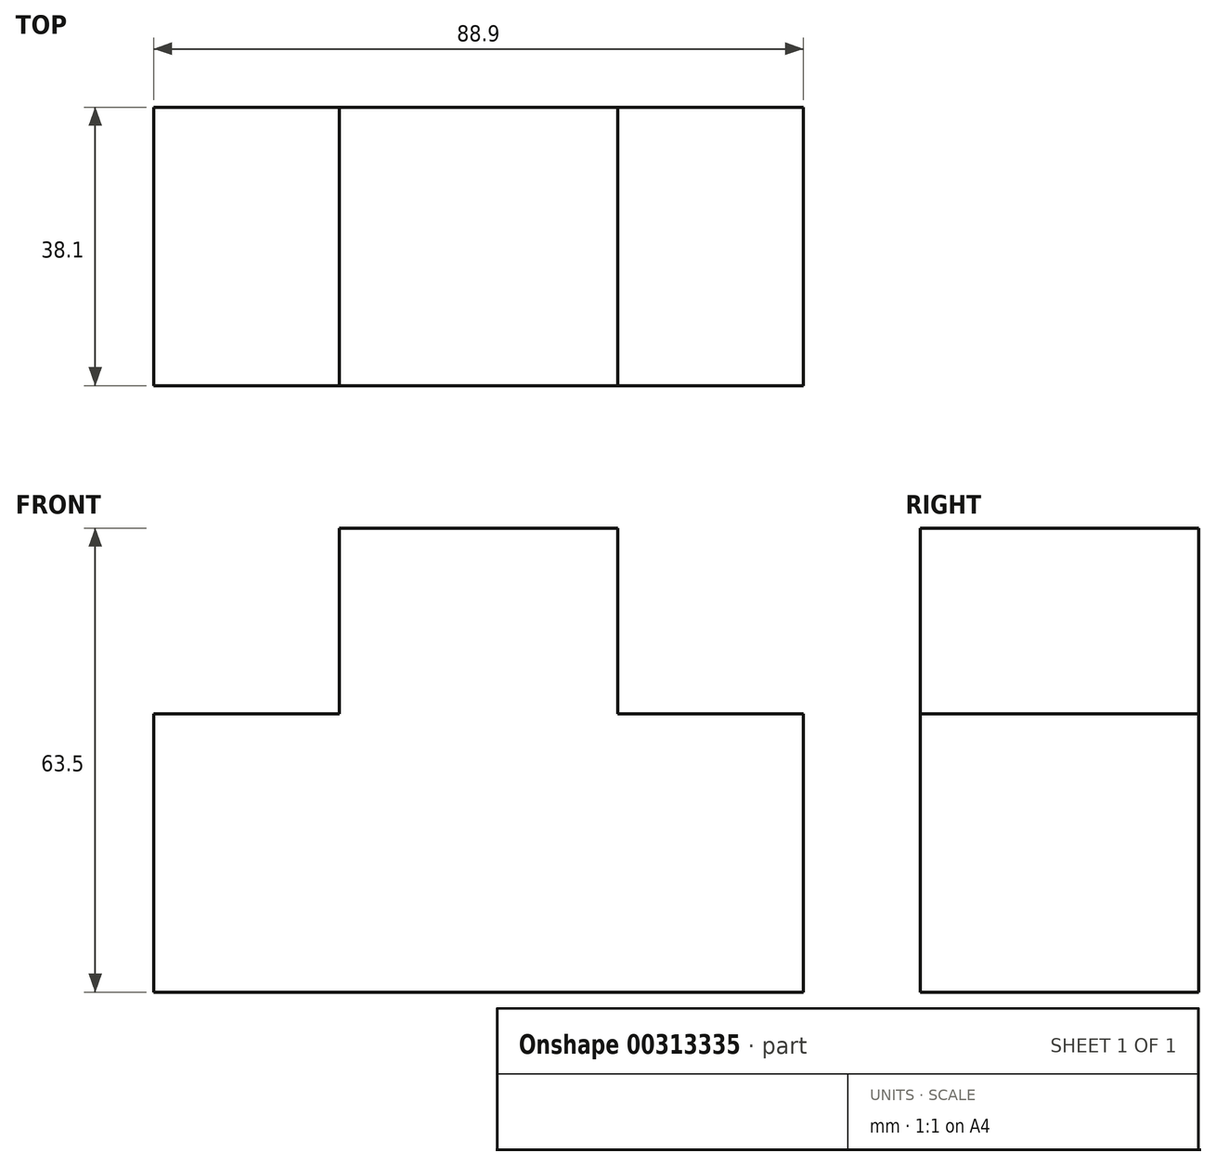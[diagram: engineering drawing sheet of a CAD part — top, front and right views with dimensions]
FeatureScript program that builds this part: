
annotation { "Feature Type Name" : "Feature", "Feature Type Description" : "" }
export const myFeature = defineFeature(function(context is Context, id is Id, definition is map)
    precondition{}
    {
        {
            var Q0;
            Q0=qCreatedBy(makeId("Front.planeOp"),FACE);
            var sketch = newSketch(context, id + "F0", { "sketchPlane" : qUnion([Q0])});
            skLineSegment(sketch, "E0", {"start": v(-20.43, 46.1) * mm, "end": v(-20.43, 71.5) * mm});
            skLineSegment(sketch, "E1", {"start": v(-20.43, 71.5) * mm, "end": v(17.67, 71.5) * mm});
            skLineSegment(sketch, "E2", {"start": v(17.67, 71.5) * mm, "end": v(17.67, 46.1) * mm});
            skLineSegment(sketch, "E3", {"start": v(17.67, 46.1) * mm, "end": v(43.07, 46.1) * mm});
            skLineSegment(sketch, "E4", {"start": v(43.07, 46.1) * mm, "end": v(43.07, 8) * mm});
            skLineSegment(sketch, "E5", {"start": v(43.07, 8) * mm, "end": v(-45.83, 8) * mm});
            skLineSegment(sketch, "E6", {"start": v(-45.83, 8) * mm, "end": v(-45.83, 46.1) * mm});
            skLineSegment(sketch, "E7", {"start": v(-45.83, 46.1) * mm, "end": v(-20.43, 46.1) * mm});
            skSolve(sketch);
        }
        {
            var Q0;
            Q0=makeQuery(id+"F0.imprint","IMPRINT",FACE,{"disambiguationData":[TD([[makeQuery(id+"F0.imprint","IMPRINT",EDGE,{"derivedFrom":sQuery(id+"F0.wireOp",EDGE,"E0")}),-1.0]])]});
            extrude(context, id + "F1", {"entities" : qUnion([Q0]), "depth" : 38.1 * mm});
        }
    });
